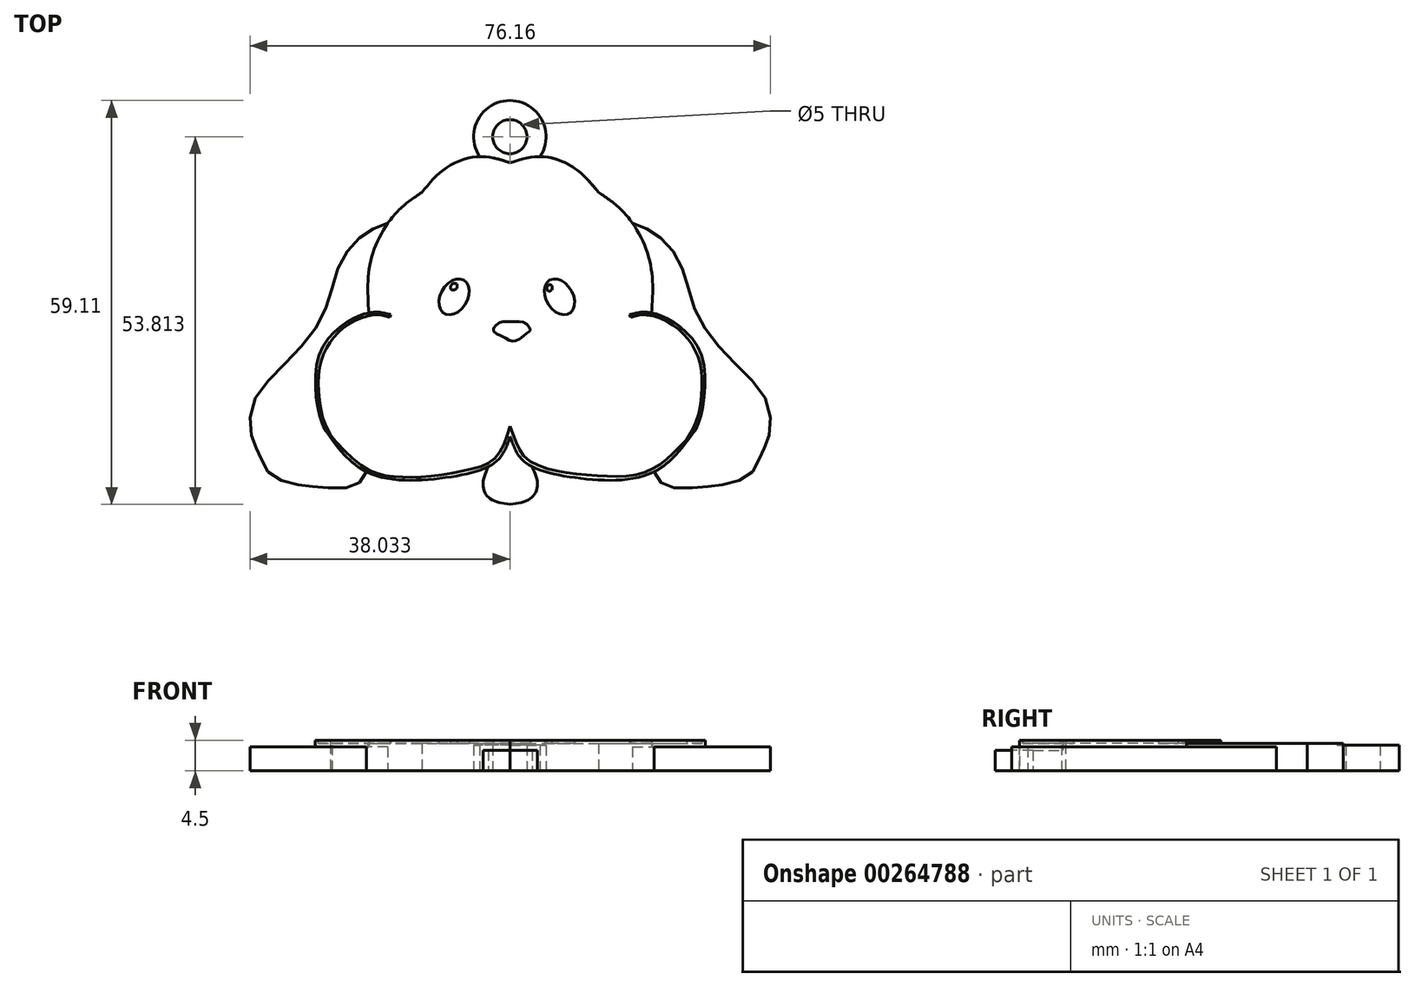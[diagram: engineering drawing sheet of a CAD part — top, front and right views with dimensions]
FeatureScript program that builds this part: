
annotation { "Feature Type Name" : "Feature", "Feature Type Description" : "" }
export const myFeature = defineFeature(function(context is Context, id is Id, definition is map)
    precondition{}
    {
        {
            var Q0;
            Q0=qCreatedBy(makeId("Top.planeOp"),FACE);
            var sketch = newSketch(context, id + "F0", { "sketchPlane" : qUnion([Q0])});
            skLineSegment(sketch, "E0", {"start": v(0, 24.47) * mm, "end": v(0, -25.53) * mm, "construction": true});
            skFitSpline(sketch, "E1", {"points": [v(0, 24.47) * mm, v(-4.54, 25.38) * mm, v(-9.44, 23.66) * mm, v(-12.92, 20.13) * mm], "startDerivative": vector(-13.71, 4.47) * mm, "endDerivative": vector(-9.36, -11.46) * mm});
            skFitSpline(sketch, "E2", {"points": [v(-12.92, 20.13) * mm, v(-16.9, 16.9) * mm, v(-20.43, 10.03) * mm, v(-20.68, 2.48) * mm], "startDerivative": vector(-14.08, -9.27) * mm, "endDerivative": vector(1.45, -21.37) * mm});
            skFitSpline(sketch, "E3", {"points": [v(-17.9, 15.62) * mm, v(-21.53, 13.88) * mm, v(-24.99, 9.5) * mm, v(-27.17, 2.67) * mm, v(-32.18, -4.18) * mm, v(-37.54, -10.52) * mm, v(-37.75, -15.88) * mm, v(-36.7, -18.23) * mm, v(-35.14, -21.1) * mm, v(-30.91, -22.65) * mm, v(-27.47, -23.03) * mm, v(-22.73, -22.8) * mm, v(-21.04, -20.75) * mm], "startDerivative": vector(-48.56, -17.69) * mm, "endDerivative": vector(20.37, 41.69) * mm});
            skFitSpline(sketch, "E4", {"points": [v(-20.68, 2.48) * mm, v(-23.72, 1.25) * mm, v(-28.09, -4.03) * mm, v(-27.74, -13.06) * mm, v(-26.54, -15.39) * mm, v(-21.04, -20.75) * mm, v(-9.54, -21.6) * mm, v(-2.07, -19.27) * mm, v(0, -15.6) * mm], "startDerivative": vector(-28.1, -3.03) * mm, "endDerivative": vector(13.34, 39.14) * mm});
            skFitSpline(sketch, "E5.MirrorCS", {"points": [v(12.92, 20.13) * mm, v(16.9, 16.9) * mm, v(20.43, 10.03) * mm, v(20.68, 2.48) * mm], "startDerivative": vector(14.08, -9.27) * mm, "endDerivative": vector(-1.45, -21.37) * mm});
            skFitSpline(sketch, "E6.MirrorCS", {"points": [v(17.9, 15.62) * mm, v(21.53, 13.88) * mm, v(24.99, 9.5) * mm, v(27.17, 2.67) * mm, v(32.18, -4.18) * mm, v(37.54, -10.52) * mm, v(37.75, -15.88) * mm, v(36.7, -18.23) * mm, v(35.14, -21.1) * mm, v(30.91, -22.65) * mm, v(27.47, -23.03) * mm, v(22.73, -22.8) * mm, v(21.04, -20.75) * mm], "startDerivative": vector(48.56, -17.69) * mm, "endDerivative": vector(-20.37, 41.69) * mm});
            skFitSpline(sketch, "E7.MirrorCS", {"points": [v(20.68, 2.48) * mm, v(23.72, 1.25) * mm, v(28.09, -4.03) * mm, v(27.74, -13.06) * mm, v(26.54, -15.39) * mm, v(21.04, -20.75) * mm, v(9.54, -21.6) * mm, v(2.07, -19.27) * mm, v(0, -15.6) * mm], "startDerivative": vector(28.1, -3.03) * mm, "endDerivative": vector(-13.34, 39.14) * mm});
            skFitSpline(sketch, "E8.MirrorCS", {"points": [v(0, 24.47) * mm, v(4.54, 25.38) * mm, v(9.44, 23.66) * mm, v(12.92, 20.13) * mm], "startDerivative": vector(13.71, 4.47) * mm, "endDerivative": vector(9.36, -11.46) * mm});
            skFitSpline(sketch, "E9", {"points": [v(-3.2, -20.01) * mm, v(-3.97, -22.22) * mm, v(-3.62, -23.96) * mm, v(-2.47, -24.96) * mm, v(0, -25.53) * mm], "startDerivative": vector(-3.83, -8.28) * mm, "endDerivative": vector(9.67, -1.47) * mm});
            skFitSpline(sketch, "E10.MirrorCS", {"points": [v(3.2, -20.01) * mm, v(3.97, -22.22) * mm, v(3.62, -23.96) * mm, v(2.47, -24.96) * mm, v(0, -25.53) * mm], "startDerivative": vector(3.83, -8.28) * mm, "endDerivative": vector(-9.67, -1.47) * mm});
            skFitSpline(sketch, "E11", {"points": [v(0, 1.22) * mm, v(-1.42, 1.12) * mm, v(-2.47, 0) * mm, v(-0.62, -1.22) * mm, v(0.67, -1.62) * mm, v(2.47, -0.47) * mm, v(2.93, 0) * mm, v(2.1, 1.04) * mm, v(0, 1.22) * mm]});
            skEllipse(sketch, "E12", {"center": v(-8.2, 4.85) * mm, "majorRadius": 2.82 * mm, "minorRadius": 1.97 * mm, "majorAxis": v(0.5, 0.86)});
            skEllipse(sketch, "E13", {"center": v(-8.23, 6.34) * mm, "majorRadius": 0.55 * mm, "minorRadius": 0.45 * mm, "majorAxis": v(0.7, 0.7)});
            skEllipse(sketch, "E14.MirrorC", {"center": v(7.2, 4.85) * mm, "majorRadius": 2.82 * mm, "minorRadius": 1.97 * mm, "majorAxis": v(-0.5, 0.86)});
            skEllipse(sketch, "E15", {"center": v(5.75, 6.14) * mm, "majorRadius": 0.48 * mm, "minorRadius": 0.4 * mm, "majorAxis": v(0.3, 0.96)});
            skFitSpline(sketch, "E16", {"points": [v(-20.68, 2.48) * mm, v(-19.38, 2.6) * mm, v(-17.47, 2.23) * mm], "startDerivative": vector(2.75, 0.5) * mm, "endDerivative": vector(3.65, -0.95) * mm});
            skFitSpline(sketch, "E17", {"points": [v(-17.47, 2.23) * mm, v(-17.6, 1.86) * mm], "startDerivative": vector(-0.14, -0.37) * mm, "endDerivative": vector(-0.14, -0.37) * mm});
            skFitSpline(sketch, "E18", {"points": [v(-17.6, 1.86) * mm, v(-19.36, 2.23) * mm, v(-22.17, 1.63) * mm, v(-24.76, 0) * mm, v(-26.6, -2.15) * mm, v(-27.8, -4.95) * mm, v(-28.03, -8.94) * mm, v(-26.97, -14.01) * mm, v(-23.2, -19.27) * mm], "startDerivative": vector(-18.43, 5.9) * mm, "endDerivative": vector(26.07, -30.2) * mm});
            skFitSpline(sketch, "E19.MirrorCS", {"points": [v(17.6, 1.86) * mm, v(19.36, 2.23) * mm, v(22.17, 1.63) * mm, v(24.76, 0) * mm, v(26.6, -2.15) * mm, v(27.8, -4.95) * mm, v(28.03, -8.94) * mm, v(26.97, -14.01) * mm, v(23.2, -19.27) * mm], "startDerivative": vector(18.43, 5.9) * mm, "endDerivative": vector(-26.07, -30.2) * mm});
            skFitSpline(sketch, "E20.MirrorCS", {"points": [v(20.68, 2.48) * mm, v(19.38, 2.6) * mm, v(17.47, 2.23) * mm], "startDerivative": vector(-2.75, 0.5) * mm, "endDerivative": vector(-3.65, -0.95) * mm});
            skFitSpline(sketch, "E21.MirrorCS", {"points": [v(17.47, 2.23) * mm, v(17.6, 1.86) * mm], "startDerivative": vector(0.14, -0.37) * mm, "endDerivative": vector(0.14, -0.37) * mm});
            skFitSpline(sketch, "E22", {"points": [v(-26.3, -15.28) * mm, v(-25.98, -15.77) * mm, v(-21.66, -19.94) * mm, v(-17.39, -21.42) * mm, v(-12.32, -21.45) * mm, v(-5.73, -20.38) * mm, v(-2.06, -18.6) * mm, v(0, -14.1) * mm], "startDerivative": vector(3.5, -6.83) * mm, "endDerivative": vector(10.5, 33.44) * mm});
            skFitSpline(sketch, "E23", {"points": [v(0, -14.1) * mm, v(1.03, -16.86) * mm, v(2.42, -18.86) * mm, v(5.67, -20.36) * mm, v(9.48, -21.06) * mm, v(13.9, -21.38) * mm, v(17.67, -21.3) * mm, v(20.94, -20.25) * mm, v(23.2, -18.64) * mm, v(25.81, -16.02) * mm], "startDerivative": vector(9.56, -27.89) * mm, "endDerivative": vector(22.95, 24.2) * mm});
            skSolve(sketch);
        }
        {
            var Q0;
            {var subQ6=sQuery(id+"F0.wireOp",EDGE,"E1");Q0=makeQuery(id+"F0.imprint","IMPRINT",FACE,{"disambiguationData":[TD([[makeQuery(id+"F0.imprint","IMPRINT",EDGE,{"derivedFrom":subQ6}),1.0]])]});}
            extrude(context, id + "F1", {"entities" : qUnion([Q0]), "depth" : 4 * mm, "offsetDistance" : 25 * mm});
        }
        {
            var Q0;
            {var subQ3=sQuery(id+"F0.wireOp",EDGE,"E3");Q0=makeQuery(id+"F0.imprint","IMPRINT",FACE,{"disambiguationData":[TD([[makeQuery(id+"F0.imprint","IMPRINT",EDGE,{"derivedFrom":subQ3}),1.0]])]});}
            var Q1;
            {var subQ3=sQuery(id+"F0.wireOp",EDGE,"E6.MirrorCS");Q1=makeQuery(id+"F0.imprint","IMPRINT",FACE,{"disambiguationData":[TD([[makeQuery(id+"F0.imprint","IMPRINT",EDGE,{"derivedFrom":subQ3}),-1.0]])]});}
            extrude(context, id + "F2", {"entities" : qUnion([Q0, Q1]), "operationType" : NewBodyOperationType.ADD, "depth" : 3.5 * mm, "offsetDistance" : 25 * mm});
        }
        {
            var Q0;
            Q0=makeQuery(id+"F0.imprint","IMPRINT",FACE,{"disambiguationData":[TD([[makeQuery(id+"F0.imprint","IMPRINT",EDGE,{"derivedFrom":sQuery(id+"F0.wireOp",EDGE,"E11")}),1.0]])]});
            var Q1;
            Q1=makeQuery(id+"F0.imprint","IMPRINT",FACE,{"disambiguationData":[TD([[makeQuery(id+"F0.imprint","IMPRINT",EDGE,{"derivedFrom":sQuery(id+"F0.wireOp",EDGE,"E12")}),1.0]])]});
            var Q2;
            Q2=makeQuery(id+"F0.imprint","IMPRINT",FACE,{"disambiguationData":[TD([[makeQuery(id+"F0.imprint","IMPRINT",EDGE,{"derivedFrom":sQuery(id+"F0.wireOp",EDGE,"E14.MirrorC")}),1.0]])]});
            extrude(context, id + "F3", {"entities" : qUnion([Q0, Q1, Q2]), "operationType" : NewBodyOperationType.ADD, "depth" : 4.5 * mm, "offsetDistance" : 25 * mm});
        }
        {
            var Q0;
            Q0=makeQuery(id+"F0.imprint","IMPRINT",FACE,{"disambiguationData":[TD([[makeQuery(id+"F0.imprint","IMPRINT",EDGE,{"derivedFrom":sQuery(id+"F0.wireOp",EDGE,"E13")}),1.0]])]});
            var Q1;
            Q1=makeQuery(id+"F0.imprint","IMPRINT",FACE,{"disambiguationData":[TD([[makeQuery(id+"F0.imprint","IMPRINT",EDGE,{"derivedFrom":sQuery(id+"F0.wireOp",EDGE,"E15")}),1.0]])]});
            extrude(context, id + "F4", {"entities" : qUnion([Q0, Q1]), "operationType" : NewBodyOperationType.ADD, "depth" : 4 * mm, "offsetDistance" : 25 * mm});
        }
        {
            var Q0;
            {var subQ3=sQuery(id+"F0.wireOp",EDGE,"E9");Q0=makeQuery(id+"F0.imprint","IMPRINT",FACE,{"disambiguationData":[TD([[makeQuery(id+"F0.imprint","IMPRINT",EDGE,{"derivedFrom":subQ3}),1.0]])]});}
            extrude(context, id + "F5", {"entities" : qUnion([Q0]), "operationType" : NewBodyOperationType.ADD, "depth" : 3 * mm, "offsetDistance" : 25 * mm});
        }
        {
            var Q0;
            Q0=qCreatedBy(makeId("Top.planeOp"),FACE);
            var sketch = newSketch(context, id + "F6", { "sketchPlane" : qUnion([Q0])});
            skCircle(sketch, "E24", {"center": v(-0.05, 28.28) * mm, "radius": 5.3 * mm});
            skCircle(sketch, "E25", {"center": v(-0.05, 28.28) * mm, "radius": 2.5 * mm});
            skLineSegment(sketch, "E26", {"start": v(-2.55, 28.28) * mm, "end": v(2.45, 28.28) * mm, "construction": true});
            skSolve(sketch);
        }
        {
            var Q0;
            Q0=makeQuery(id+"F6.imprint","IMPRINT",FACE,{"disambiguationData":[TD([[makeQuery(id+"F6.imprint","IMPRINT",EDGE,{"derivedFrom":sQuery(id+"F6.wireOp",EDGE,"E24")}),1.0]])]});
            extrude(context, id + "F7", {"entities" : qUnion([Q0]), "operationType" : NewBodyOperationType.ADD, "depth" : 3.75 * mm, "offsetDistance" : 25 * mm});
        }
        {
            var Q0;
            {var subQ0=sQuery(id+"F0.wireOp",EDGE,"E16");Q0=makeQuery(id+"F0.imprint","IMPRINT",FACE,{"disambiguationData":[TD([[makeQuery(id+"F0.imprint","IMPRINT",EDGE,{"derivedFrom":subQ0}),-1.0]])]});}
            var Q1;
            {var subQ2=sQuery(id+"F0.wireOp",EDGE,"E19.MirrorCS");Q1=makeQuery(id+"F0.imprint","IMPRINT",FACE,{"disambiguationData":[TD([[makeQuery(id+"F0.imprint","IMPRINT",EDGE,{"derivedFrom":subQ2}),1.0]])]});}
            var Q2;
            {var subQ4=sQuery(id+"F0.wireOp",EDGE,"E23");Q2=makeQuery(id+"F0.imprint","IMPRINT",FACE,{"disambiguationData":[TD([[makeQuery(id+"F0.imprint","IMPRINT",EDGE,{"derivedFrom":subQ4}),-1.0]])]});}
            extrude(context, id + "F8", {"entities" : qUnion([Q0, Q1, Q2]), "operationType" : NewBodyOperationType.ADD, "depth" : 4.5 * mm, "offsetDistance" : 25 * mm});
        }
    });
